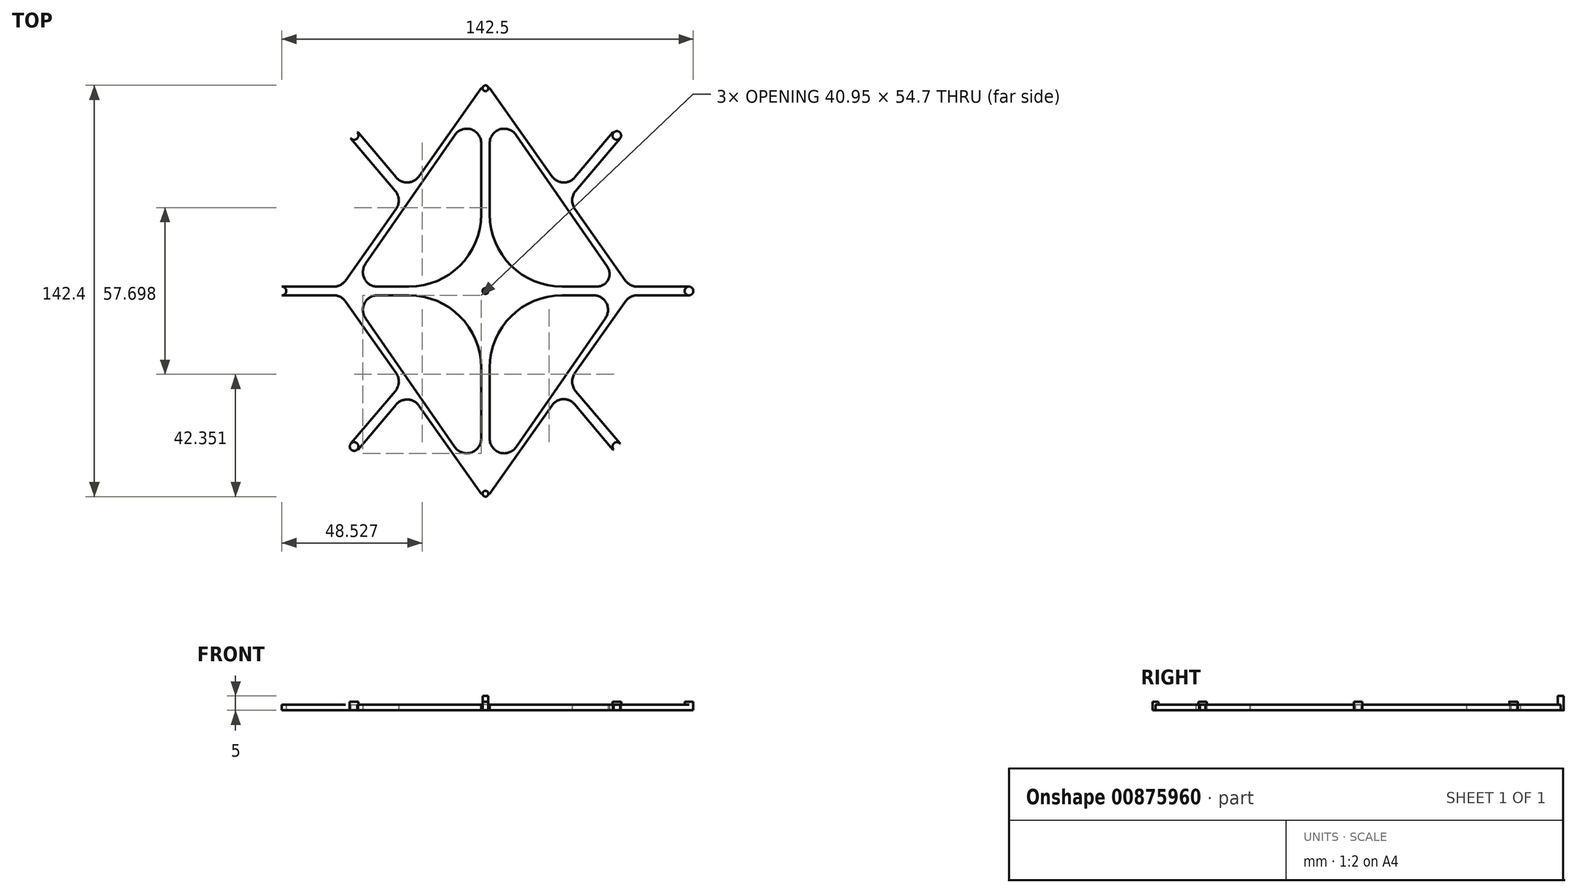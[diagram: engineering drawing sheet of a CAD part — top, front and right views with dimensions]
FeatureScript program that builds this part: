
annotation { "Feature Type Name" : "Feature", "Feature Type Description" : "" }
export const myFeature = defineFeature(function(context is Context, id is Id, definition is map)
    precondition{}
    {
        {
            var Q0;
            Q0=qCreatedBy(makeId("Top.planeOp"),FACE);
            var sketch = newSketch(context, id + "F0", { "sketchPlane" : qUnion([Q0])});
            skLineSegment(sketch, "E0.top", {"start": v(1.5, -35.1) * mm, "end": v(1, -35.1) * mm});
            skLineSegment(sketch, "E0.left", {"start": v(1.5, 8.6) * mm, "end": v(1.5, -16.1) * mm});
            skPoint(sketch, "E0.middle", {"position": v(0, 0) * mm});
            skCircle(sketch, "E1", {"center": v(0, 35.1) * mm, "radius": 1 * mm});
            skCircle(sketch, "E2", {"center": v(0, -35.1) * mm, "radius": 1 * mm});
            skPoint(sketch, "E2.perimeterSnap0", {"position": v(0, -35.1) * mm});
            skLineSegment(sketch, "E3", {"start": v(1, -35.1) * mm, "end": v(1.5, -35.1) * mm});
            skPoint(sketch, "E4.trimOffspring.end.orphan", {"position": v(-1.5, -35.1) * mm});
            skPoint(sketch, "E5.start.orphan", {"position": v(0, -34.1) * mm});
            skLineSegment(sketch, "E6", {"start": v(-1.5, -35.1) * mm, "end": v(-1, -35.1) * mm});
            skLineSegment(sketch, "E7", {"start": v(-1.5, 8.6) * mm, "end": v(-1.5, -16.1) * mm});
            skLineSegment(sketch, "E8", {"start": v(-1.5, 61.6) * mm, "end": v(-1.5, 86.3) * mm});
            skLineSegment(sketch, "E9", {"start": v(1.5, 61.6) * mm, "end": v(1.5, 86.3) * mm});
            skLineSegment(sketch, "E10", {"start": v(1.5, 105.3) * mm, "end": v(1, 105.3) * mm});
            skLineSegment(sketch, "E11", {"start": v(-1.5, 105.3) * mm, "end": v(-1, 105.3) * mm});
            skCircle(sketch, "E12", {"center": v(0, 105.3) * mm, "radius": 1 * mm});
            skLineSegment(sketch, "E13", {"start": v(26.5, 33.6) * mm, "end": v(37.46, 33.6) * mm});
            skLineSegment(sketch, "E14", {"start": v(26.5, 36.6) * mm, "end": v(38.55, 36.6) * mm});
            skLineSegment(sketch, "E15", {"start": v(-26.5, 36.6) * mm, "end": v(-37.46, 36.6) * mm});
            skLineSegment(sketch, "E16", {"start": v(-26.5, 33.6) * mm, "end": v(-37.46, 33.6) * mm});
            skLineSegment(sketch, "E17", {"start": v(42.2, 43.55) * mm, "end": v(10.61, 89.14) * mm});
            skLineSegment(sketch, "E18", {"start": v(1.5, 105.3) * mm, "end": v(23.04, 74.78) * mm});
            skLineSegment(sketch, "E19.MirrorCS", {"start": v(1.5, -35.1) * mm, "end": v(23.2, -4.37) * mm});
            skLineSegment(sketch, "E20.MirrorCS", {"start": v(41.57, 25.75) * mm, "end": v(10.61, -18.94) * mm});
            skLineSegment(sketch, "E21.MirrorCS", {"start": v(-41.57, 44.45) * mm, "end": v(-10.61, 89.14) * mm});
            skLineSegment(sketch, "E22.MirrorCS", {"start": v(-1.5, 105.3) * mm, "end": v(-23.04, 74.78) * mm});
            skLineSegment(sketch, "E23.MirrorCS", {"start": v(-1.5, -35.1) * mm, "end": v(-23.04, -4.58) * mm});
            skLineSegment(sketch, "E24.MirrorCS", {"start": v(-41.57, 25.75) * mm, "end": v(-10.61, -18.94) * mm});
            skPoint(sketch, "E0.bottom.start.orphan", {"position": v(1.5, 35.1) * mm});
            skPoint(sketch, "E25.trimOffspring.end.orphan", {"position": v(-1.5, 35.1) * mm});
            skPoint(sketch, "E26.start.orphan", {"position": v(0, 34.1) * mm});
            skPoint(sketch, "E27.end.orphan", {"position": v(0, 36.6) * mm});
            skPoint(sketch, "E27.start.orphan", {"position": v(0, 36.1) * mm});
            skPoint(sketch, "E28.visualSharp", {"position": v(1.5, 36.6) * mm});
            skArc(sketch, "E28.filletArc", {"start": v(1.5, 61.6) * mm, "mid": v(8.82, 43.92) * mm, "end": v(26.5, 36.6) * mm});
            skPoint(sketch, "E29.visualSharp", {"position": v(47, 36.6) * mm});
            skArc(sketch, "E29.filletArc", {"start": v(38.55, 36.6) * mm, "mid": v(42.47, 38.97) * mm, "end": v(42.2, 43.55) * mm});
            skPoint(sketch, "E30.visualSharp", {"position": v(1.5, 102.3) * mm});
            skArc(sketch, "E30.filletArc", {"start": v(10.61, 89.14) * mm, "mid": v(5, 91.07) * mm, "end": v(1.5, 86.3) * mm});
            skPoint(sketch, "E31.visualSharp", {"position": v(-1.5, 102.3) * mm});
            skArc(sketch, "E31.filletArc", {"start": v(-1.5, 86.3) * mm, "mid": v(-5, 91.07) * mm, "end": v(-10.61, 89.14) * mm});
            skPoint(sketch, "E32.visualSharp", {"position": v(-47, 36.6) * mm});
            skArc(sketch, "E32.filletArc", {"start": v(-41.57, 44.45) * mm, "mid": v(-41.88, 39.28) * mm, "end": v(-37.46, 36.6) * mm});
            skPoint(sketch, "E33.visualSharp", {"position": v(-47, 33.6) * mm});
            skArc(sketch, "E33.filletArc", {"start": v(-37.46, 33.6) * mm, "mid": v(-41.88, 30.92) * mm, "end": v(-41.57, 25.75) * mm});
            skPoint(sketch, "E34.visualSharp", {"position": v(47, 33.6) * mm});
            skArc(sketch, "E34.filletArc", {"start": v(41.57, 25.75) * mm, "mid": v(41.88, 30.92) * mm, "end": v(37.46, 33.6) * mm});
            skPoint(sketch, "E35.visualSharp", {"position": v(1.5, -32.1) * mm});
            skArc(sketch, "E35.filletArc", {"start": v(1.5, -16.1) * mm, "mid": v(5, -20.87) * mm, "end": v(10.61, -18.94) * mm});
            skPoint(sketch, "E36.visualSharp", {"position": v(-1.5, -32.1) * mm});
            skArc(sketch, "E36.filletArc", {"start": v(-10.61, -18.94) * mm, "mid": v(-5, -20.87) * mm, "end": v(-1.5, -16.1) * mm});
            skPoint(sketch, "E37.visualSharp", {"position": v(-1.5, 36.6) * mm});
            skArc(sketch, "E37.filletArc", {"start": v(-26.5, 36.6) * mm, "mid": v(-8.82, 43.92) * mm, "end": v(-1.5, 61.6) * mm});
            skPoint(sketch, "E38.visualSharp", {"position": v(-1.5, 33.6) * mm});
            skArc(sketch, "E38.filletArc", {"start": v(-1.5, 8.6) * mm, "mid": v(-8.82, 26.28) * mm, "end": v(-26.5, 33.6) * mm});
            skPoint(sketch, "E39.visualSharp", {"position": v(1.5, 33.6) * mm});
            skArc(sketch, "E39.filletArc", {"start": v(26.5, 33.6) * mm, "mid": v(8.82, 26.28) * mm, "end": v(1.5, 8.6) * mm});
            skLineSegment(sketch, "E40", {"start": v(0, 35.1) * mm, "end": v(1.5, 35.1) * mm});
            skLineSegment(sketch, "E41.bottom", {"start": v(52.6, 33.6) * mm, "end": v(70.5, 33.6) * mm});
            skLineSegment(sketch, "E41.top", {"start": v(52.6, 36.6) * mm, "end": v(70.5, 36.6) * mm});
            skCircle(sketch, "E42", {"center": v(70.5, 35.1) * mm, "radius": 1.5 * mm});
            skLineSegment(sketch, "E43.MirrorCS", {"start": v(-52.6, 33.6) * mm, "end": v(-70.5, 33.6) * mm});
            skLineSegment(sketch, "E44.MirrorCS", {"start": v(-52.6, 36.6) * mm, "end": v(-70.5, 36.6) * mm});
            skCircle(sketch, "E45.MirrorC", {"center": v(-70.5, 35.1) * mm, "radius": 1.5 * mm});
            skArc(sketch, "E46.filletArc", {"start": v(-52.6, 36.6) * mm, "mid": v(-50.3, 37.16) * mm, "end": v(-48.5, 38.72) * mm});
            skPoint(sketch, "E47.visualSharp", {"position": v(-50, 33.6) * mm});
            skArc(sketch, "E47.filletArc", {"start": v(-48.5, 31.48) * mm, "mid": v(-50.3, 33.04) * mm, "end": v(-52.6, 33.6) * mm});
            skPoint(sketch, "E48.visualSharp", {"position": v(50, 36.6) * mm});
            skArc(sketch, "E48.filletArc", {"start": v(48.5, 38.72) * mm, "mid": v(50.3, 37.16) * mm, "end": v(52.6, 36.6) * mm});
            skPoint(sketch, "E49.visualSharp", {"position": v(50, 33.6) * mm});
            skArc(sketch, "E49.filletArc", {"start": v(52.6, 33.6) * mm, "mid": v(50.3, 33.04) * mm, "end": v(48.5, 31.48) * mm});
            skLineSegment(sketch, "E50", {"start": v(46.65, 87.98) * mm, "end": v(31.2, 69.7) * mm});
            skLineSegment(sketch, "E51", {"start": v(44.16, 90.08) * mm, "end": v(30.95, 74.44) * mm});
            skLineSegment(sketch, "E52.trimOffspring", {"start": v(30.94, 63.6) * mm, "end": v(48.5, 38.72) * mm});
            skPoint(sketch, "E53.orphan", {"position": v(26.4, 66.34) * mm});
            skCircle(sketch, "E54", {"center": v(45.5, 88.95) * mm, "radius": 1.5 * mm});
            skLineSegment(sketch, "E55.MirrorCS", {"start": v(46.65, -17.78) * mm, "end": v(31.2, 0.5) * mm});
            skLineSegment(sketch, "E56.MirrorCS", {"start": v(44.16, -19.88) * mm, "end": v(30.78, -4.04) * mm});
            skCircle(sketch, "E57.MirrorC", {"center": v(45.5, -18.75) * mm, "radius": 1.5 * mm});
            skLineSegment(sketch, "E58.MirrorCS", {"start": v(-46.65, 87.98) * mm, "end": v(-31.2, 69.7) * mm});
            skCircle(sketch, "E59.MirrorC", {"center": v(-45.5, 88.95) * mm, "radius": 1.5 * mm});
            skLineSegment(sketch, "E60.MirrorCS", {"start": v(-44.16, 90.08) * mm, "end": v(-30.95, 74.44) * mm});
            skLineSegment(sketch, "E61.MirrorCS", {"start": v(-44.16, -19.88) * mm, "end": v(-30.95, -4.24) * mm});
            skLineSegment(sketch, "E62.MirrorCS", {"start": v(-46.65, -17.78) * mm, "end": v(-31.2, 0.5) * mm});
            skCircle(sketch, "E63.MirrorC", {"center": v(-45.5, -18.75) * mm, "radius": 1.5 * mm});
            skLineSegment(sketch, "E64.trimOffspring", {"start": v(-30.94, 6.6) * mm, "end": v(-48.5, 31.48) * mm});
            skLineSegment(sketch, "E65.trimOffspring", {"start": v(30.94, 6.6) * mm, "end": v(48.5, 31.48) * mm});
            skLineSegment(sketch, "E66.trimOffspring", {"start": v(-30.94, 63.6) * mm, "end": v(-48.5, 38.72) * mm});
            skPoint(sketch, "E67.end.orphan", {"position": v(0, -36.6) * mm});
            skPoint(sketch, "E67.start.orphan", {"position": v(0, -36.1) * mm});
            skPoint(sketch, "E68.visualSharp", {"position": v(28.71, 3.44) * mm});
            skArc(sketch, "E68.filletArc", {"start": v(30.94, 6.6) * mm, "mid": v(30.03, 3.5) * mm, "end": v(31.2, 0.5) * mm});
            skPoint(sketch, "E69.visualSharp", {"position": v(26.77, 0.7) * mm});
            skArc(sketch, "E69.filletArc", {"start": v(30.78, -4.04) * mm, "mid": v(26.9, -2.34) * mm, "end": v(23.2, -4.37) * mm});
            skPoint(sketch, "E70.visualSharp", {"position": v(28.71, 66.76) * mm});
            skArc(sketch, "E70.filletArc", {"start": v(31.2, 69.7) * mm, "mid": v(30.03, 66.7) * mm, "end": v(30.94, 63.6) * mm});
            skPoint(sketch, "E71.visualSharp", {"position": v(26.77, 69.5) * mm});
            skArc(sketch, "E71.filletArc", {"start": v(23.04, 74.78) * mm, "mid": v(26.91, 72.67) * mm, "end": v(30.95, 74.44) * mm});
            skPoint(sketch, "E72.visualSharp", {"position": v(-26.77, 69.5) * mm});
            skArc(sketch, "E72.filletArc", {"start": v(-30.95, 74.44) * mm, "mid": v(-26.91, 72.67) * mm, "end": v(-23.04, 74.78) * mm});
            skPoint(sketch, "E73.visualSharp", {"position": v(-28.71, 66.76) * mm});
            skArc(sketch, "E73.filletArc", {"start": v(-30.94, 63.6) * mm, "mid": v(-30.03, 66.7) * mm, "end": v(-31.2, 69.7) * mm});
            skPoint(sketch, "E74.visualSharp", {"position": v(-26.77, 0.7) * mm});
            skArc(sketch, "E74.filletArc", {"start": v(-23.04, -4.58) * mm, "mid": v(-26.91, -2.47) * mm, "end": v(-30.95, -4.24) * mm});
            skPoint(sketch, "E75.visualSharp", {"position": v(-28.71, 3.44) * mm});
            skArc(sketch, "E75.filletArc", {"start": v(-31.2, 0.5) * mm, "mid": v(-30.03, 3.5) * mm, "end": v(-30.94, 6.6) * mm});
            skLineSegment(sketch, "E76", {"start": v(44.16, 90.08) * mm, "end": v(44.36, 89.92) * mm});
            skLineSegment(sketch, "E77", {"start": v(-44.16, 90.08) * mm, "end": v(-44.36, 89.92) * mm});
            skLineSegment(sketch, "E78", {"start": v(-44.16, -19.88) * mm, "end": v(-44.36, -19.72) * mm});
            skLineSegment(sketch, "E79", {"start": v(44.16, -19.88) * mm, "end": v(44.36, -19.72) * mm});
            skSolve(sketch);
        }
        {
            var Q0;
            Q0=makeQuery(id+"F0.imprint","IMPRINT",FACE,{"disambiguationData":[TD([[makeQuery(id+"F0.imprint","IMPRINT",EDGE,{"derivedFrom":sQuery(id+"F0.wireOp",EDGE,"E0.left")}),-1.0]])]});
            extrude(context, id + "F1", {"entities" : qUnion([Q0]), "depth" : 2 * mm, "offsetDistance" : 25 * mm});
        }
        {
            var Q0;
            {var subQ0=sQuery(id+"F0.wireOp",EDGE,"E59.MirrorC");var subQ1=makeQuery(id+"F0.imprint","INTERSECT",VERTEX,{"derivedFrom":[sQuery(id+"F0.wireOp",EDGE,"E58.MirrorCS"),subQ0]});Q0=makeQuery(id+"F0.imprint","IMPRINT",FACE,{"disambiguationData":[TD([[makeQuery(id+"F0.imprint","IMPRINT",EDGE,{"disambiguationData":[TD([[subQ1,1.0]])],"derivedFrom":subQ0}),-1.0]])]});}
            var Q1;
            {var subQ0=sQuery(id+"F0.wireOp",EDGE,"E12");var subQ1=makeQuery(id+"F0.imprint","INTERSECT",VERTEX,{"derivedFrom":[sQuery(id+"F0.wireOp",EDGE,"E10"),subQ0]});Q1=makeQuery(id+"F0.imprint","IMPRINT",FACE,{"disambiguationData":[TD([[makeQuery(id+"F0.imprint","IMPRINT",EDGE,{"disambiguationData":[TD([[subQ1,-1.0]])],"derivedFrom":subQ0}),1.0]])]});}
            var Q2;
            {var subQ0=sQuery(id+"F0.wireOp",EDGE,"E54");var subQ1=makeQuery(id+"F0.imprint","INTERSECT",VERTEX,{"derivedFrom":[sQuery(id+"F0.wireOp",EDGE,"E50"),subQ0]});Q2=makeQuery(id+"F0.imprint","IMPRINT",FACE,{"disambiguationData":[TD([[makeQuery(id+"F0.imprint","IMPRINT",EDGE,{"disambiguationData":[TD([[subQ1,1.0]])],"derivedFrom":subQ0}),1.0]])]});}
            var Q3;
            {var subQ0=sQuery(id+"F0.wireOp",EDGE,"E42");var subQ1=makeQuery(id+"F0.imprint","INTERSECT",VERTEX,{"derivedFrom":[sQuery(id+"F0.wireOp",EDGE,"E41.bottom"),subQ0]});Q3=makeQuery(id+"F0.imprint","IMPRINT",FACE,{"disambiguationData":[TD([[makeQuery(id+"F0.imprint","IMPRINT",EDGE,{"disambiguationData":[TD([[subQ1,1.0]])],"derivedFrom":subQ0}),1.0]])]});}
            var Q4;
            {var subQ0=sQuery(id+"F0.wireOp",EDGE,"E57.MirrorC");var subQ1=makeQuery(id+"F0.imprint","INTERSECT",VERTEX,{"derivedFrom":[sQuery(id+"F0.wireOp",EDGE,"E55.MirrorCS"),subQ0]});Q4=makeQuery(id+"F0.imprint","IMPRINT",FACE,{"disambiguationData":[TD([[makeQuery(id+"F0.imprint","IMPRINT",EDGE,{"disambiguationData":[TD([[subQ1,1.0]])],"derivedFrom":subQ0}),-1.0]])]});}
            var Q5;
            {var subQ0=sQuery(id+"F0.wireOp",EDGE,"E2");var subQ1=makeQuery(id+"F0.imprint","INTERSECT",VERTEX,{"derivedFrom":[subQ0,sQuery(id+"F0.wireOp",EDGE,"E3")]});Q5=makeQuery(id+"F0.imprint","IMPRINT",FACE,{"disambiguationData":[TD([[makeQuery(id+"F0.imprint","IMPRINT",EDGE,{"disambiguationData":[TD([[subQ1,-1.0]])],"derivedFrom":subQ0}),1.0]])]});}
            var Q6;
            {var subQ0=sQuery(id+"F0.wireOp",EDGE,"E63.MirrorC");var subQ1=makeQuery(id+"F0.imprint","INTERSECT",VERTEX,{"derivedFrom":[sQuery(id+"F0.wireOp",EDGE,"E62.MirrorCS"),subQ0]});Q6=makeQuery(id+"F0.imprint","IMPRINT",FACE,{"disambiguationData":[TD([[makeQuery(id+"F0.imprint","IMPRINT",EDGE,{"disambiguationData":[TD([[subQ1,1.0]])],"derivedFrom":subQ0}),1.0]])]});}
            extrude(context, id + "F2", {"entities" : qUnion([Q0, Q1, Q2, Q3, Q4, Q5, Q6]), "operationType" : NewBodyOperationType.ADD, "depth" : 3 * mm, "offsetDistance" : 25 * mm});
        }
        {
            var Q0;
            {var subQ0=sQuery(id+"F0.wireOp",EDGE,"E12");var subQ1=makeQuery(id+"F0.imprint","INTERSECT",VERTEX,{"derivedFrom":[sQuery(id+"F0.wireOp",EDGE,"E10"),subQ0]});Q0=makeQuery(id+"F0.imprint","IMPRINT",FACE,{"disambiguationData":[TD([[makeQuery(id+"F0.imprint","IMPRINT",EDGE,{"disambiguationData":[TD([[subQ1,-1.0]])],"derivedFrom":subQ0}),1.0]])]});}
            extrude(context, id + "F3", {"entities" : qUnion([Q0]), "operationType" : NewBodyOperationType.ADD, "depth" : 5 * mm, "offsetDistance" : 25 * mm});
        }
    });
